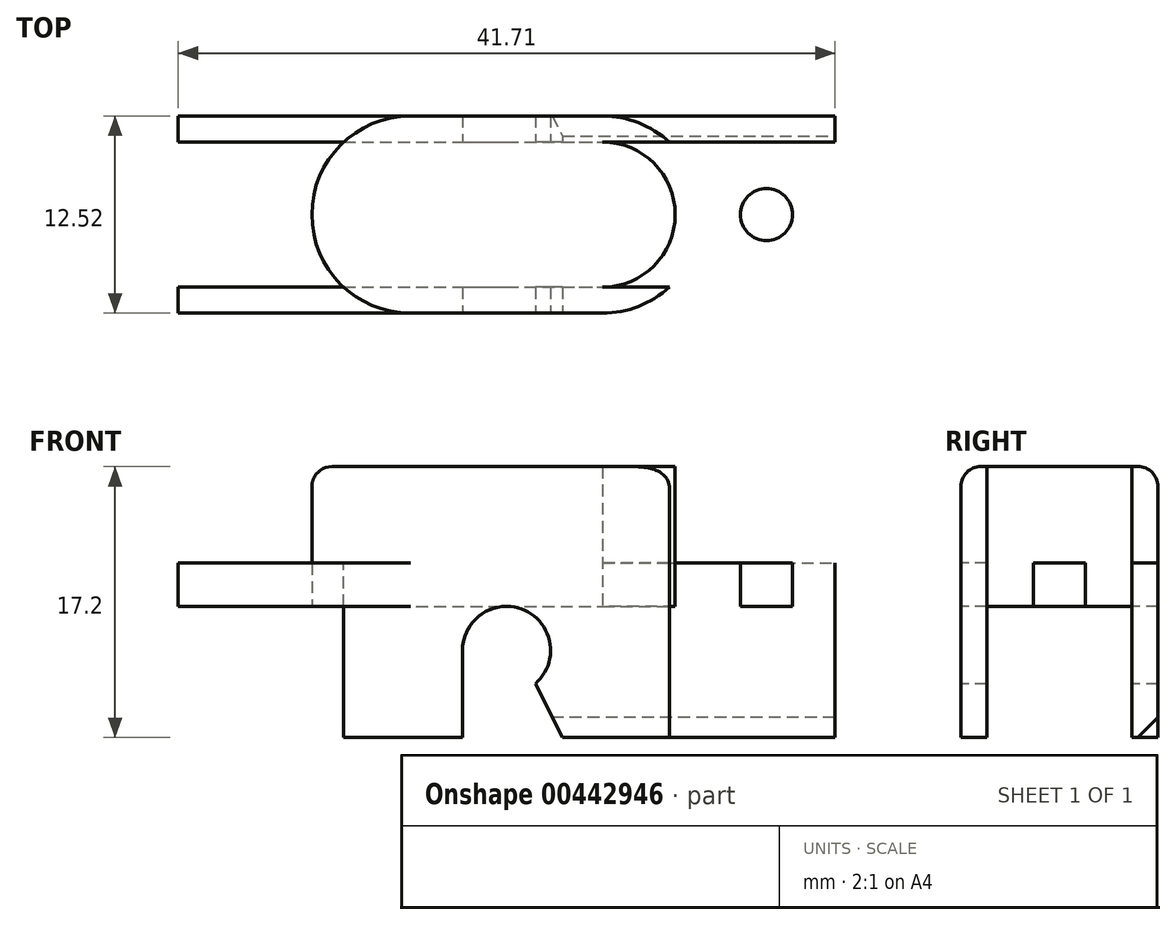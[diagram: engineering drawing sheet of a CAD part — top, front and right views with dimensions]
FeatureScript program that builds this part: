
annotation { "Feature Type Name" : "Feature", "Feature Type Description" : "" }
export const myFeature = defineFeature(function(context is Context, id is Id, definition is map)
    precondition{}
    {
        {
            var Q0;
            Q0=qCreatedBy(makeId("Top.planeOp"),FACE);
            var sketch = newSketch(context, id + "F0", { "sketchPlane" : qUnion([Q0])});
            skLineSegment(sketch, "E0.bottom", {"start": v(0, 12.52) * mm, "end": v(41.7, 12.52) * mm});
            skLineSegment(sketch, "E0.top", {"start": v(0, 0) * mm, "end": v(41.7, 0) * mm});
            skLineSegment(sketch, "E0.left", {"start": v(0, 12.52) * mm, "end": v(0, 0) * mm});
            skLineSegment(sketch, "E0.right", {"start": v(41.7, 12.52) * mm, "end": v(41.7, 0) * mm});
            skCircle(sketch, "E1", {"center": v(4.34, 6.26) * mm, "radius": 1.65 * mm});
            skPoint(sketch, "E2", {"position": v(20.85, 12.52) * mm});
            skPoint(sketch, "E3", {"position": v(20.85, 0) * mm});
            skPoint(sketch, "E4", {"position": v(0, 6.26) * mm});
            skPoint(sketch, "E5", {"position": v(41.7, 6.26) * mm});
            skLineSegment(sketch, "E6.bottom", {"start": v(14.75, 12.52) * mm, "end": v(20.85, 12.52) * mm});
            skLineSegment(sketch, "E6.top", {"start": v(14.75, 0) * mm, "end": v(20.85, 0) * mm});
            skArc(sketch, "E7", {"start": v(14.75, 12.52) * mm, "mid": v(8.49, 6.26) * mm, "end": v(14.75, 0) * mm});
            skPoint(sketch, "E8", {"position": v(8.49, 6.26) * mm});
            skPoint(sketch, "E9", {"position": v(33.22, 6.26) * mm});
            skLineSegment(sketch, "E10", {"start": v(20.85, 12.52) * mm, "end": v(20.85, 0) * mm, "construction": true});
            skLineSegment(sketch, "E11", {"start": v(0, 6.26) * mm, "end": v(41.7, 6.26) * mm, "construction": true});
            skPoint(sketch, "E12", {"position": v(20.85, 6.26) * mm});
            skCircle(sketch, "E13.MirrorC", {"center": v(37.36, 6.26) * mm, "radius": 1.65 * mm});
            skArc(sketch, "E14.0", {"start": v(14.75, 10.87) * mm, "mid": v(10.14, 6.26) * mm, "end": v(14.75, 1.65) * mm});
            skLineSegment(sketch, "E14.1", {"start": v(14.75, 10.87) * mm, "end": v(20.85, 10.87) * mm});
            skLineSegment(sketch, "E14.3", {"start": v(14.75, 1.65) * mm, "end": v(20.85, 1.65) * mm});
            skPoint(sketch, "E15", {"position": v(10.14, 6.26) * mm});
            skLineSegment(sketch, "E16.MirrorCS", {"start": v(26.96, 10.87) * mm, "end": v(20.85, 10.87) * mm});
            skArc(sketch, "E17.MirrorCS", {"start": v(26.96, 10.87) * mm, "mid": v(31.57, 6.26) * mm, "end": v(26.96, 1.65) * mm});
            skLineSegment(sketch, "E18.MirrorCS", {"start": v(26.96, 1.65) * mm, "end": v(20.85, 1.65) * mm});
            skLineSegment(sketch, "E19.MirrorCS", {"start": v(26.96, 0) * mm, "end": v(20.85, 0) * mm});
            skArc(sketch, "E20.MirrorCS", {"start": v(26.96, 12.52) * mm, "mid": v(33.22, 6.26) * mm, "end": v(26.96, 0) * mm});
            skLineSegment(sketch, "E21.MirrorCS", {"start": v(26.96, 12.52) * mm, "end": v(20.85, 12.52) * mm});
            skPoint(sketch, "E22", {"position": v(31.57, 6.26) * mm});
            skPoint(sketch, "E23", {"position": v(41.7, 1.65) * mm});
            skLineSegment(sketch, "E24.top", {"start": v(0, 1.65) * mm, "end": v(41.7, 1.65) * mm});
            skLineSegment(sketch, "E24.left", {"start": v(0, 0) * mm, "end": v(0, 1.65) * mm});
            skLineSegment(sketch, "E24.right", {"start": v(41.7, 0) * mm, "end": v(41.7, 1.65) * mm});
            skLineSegment(sketch, "E25.MirrorCS", {"start": v(0, 12.52) * mm, "end": v(0, 10.87) * mm});
            skLineSegment(sketch, "E26.MirrorCS", {"start": v(0, 10.87) * mm, "end": v(41.7, 10.87) * mm});
            skSolve(sketch);
        }
        {
            var Q0;
            {var subQ0=sQuery(id+"F0.wireOp",EDGE,"E0.top");var subQ1=sQuery(id+"F0.wireOp",EDGE,"E7");var subQ2=makeQuery(id+"F0.imprint","INTERSECT",VERTEX,{"derivedFrom":[subQ1,subQ0]});Q0=makeQuery(id+"F0.imprint","IMPRINT",FACE,{"disambiguationData":[TD([[makeQuery(id+"F0.imprint","IMPRINT",EDGE,{"disambiguationData":[TD([[subQ2,1.0]])],"derivedFrom":subQ1}),1.0]])]});}
            var Q1;
            {var subQ5=sQuery(id+"F0.wireOp",EDGE,"E14.0");Q1=makeQuery(id+"F0.imprint","IMPRINT",FACE,{"disambiguationData":[TD([[makeQuery(id+"F0.imprint","IMPRINT",EDGE,{"derivedFrom":subQ5}),-1.0]])]});}
            var Q2;
            {var subQ2=sQuery(id+"F0.wireOp",EDGE,"E7");var subQ4=sQuery(id+"F0.wireOp",EDGE,"E0.bottom");var subQ8=makeQuery(id+"F0.imprint","INTERSECT",VERTEX,{"derivedFrom":[subQ2,subQ4]});Q2=makeQuery(id+"F0.imprint","IMPRINT",FACE,{"disambiguationData":[TD([[makeQuery(id+"F0.imprint","IMPRINT",EDGE,{"disambiguationData":[TD([[subQ8,-1.0]])],"derivedFrom":subQ2}),1.0]])]});}
            var Q3;
            {var subQ0=sQuery(id+"F0.wireOp",EDGE,"E17.MirrorCS");Q3=makeQuery(id+"F0.imprint","IMPRINT",FACE,{"disambiguationData":[TD([[makeQuery(id+"F0.imprint","IMPRINT",EDGE,{"derivedFrom":subQ0}),1.0]])]});}
            extrude(context, id + "F1", {"entities" : qUnion([Q0, Q1, Q2, Q3]), "depth" : 6.13 * mm});
        }
        {
            var Q0;
            {var subQ5=sQuery(id+"F0.wireOp",EDGE,"E24.left");Q0=makeQuery(id+"F0.imprint","IMPRINT",FACE,{"disambiguationData":[TD([[makeQuery(id+"F0.imprint","IMPRINT",EDGE,{"derivedFrom":subQ5}),-1.0]])]});}
            var Q1;
            {var subQ0=sQuery(id+"F0.wireOp",EDGE,"E0.top");var subQ1=sQuery(id+"F0.wireOp",EDGE,"E7");var subQ2=makeQuery(id+"F0.imprint","INTERSECT",VERTEX,{"derivedFrom":[subQ1,subQ0]});Q1=makeQuery(id+"F0.imprint","IMPRINT",FACE,{"disambiguationData":[TD([[makeQuery(id+"F0.imprint","IMPRINT",EDGE,{"disambiguationData":[TD([[subQ2,1.0]])],"derivedFrom":subQ1}),1.0]])]});}
            var Q2;
            {var subQ5=sQuery(id+"F0.wireOp",EDGE,"E24.right");Q2=makeQuery(id+"F0.imprint","IMPRINT",FACE,{"disambiguationData":[TD([[makeQuery(id+"F0.imprint","IMPRINT",EDGE,{"derivedFrom":subQ5}),1.0]])]});}
            var Q3;
            {var subQ5=sQuery(id+"F0.wireOp",EDGE,"E25.MirrorCS");Q3=makeQuery(id+"F0.imprint","IMPRINT",FACE,{"disambiguationData":[TD([[makeQuery(id+"F0.imprint","IMPRINT",EDGE,{"derivedFrom":subQ5}),1.0]])]});}
            var Q4;
            {var subQ2=sQuery(id+"F0.wireOp",EDGE,"E7");var subQ4=sQuery(id+"F0.wireOp",EDGE,"E0.bottom");var subQ8=makeQuery(id+"F0.imprint","INTERSECT",VERTEX,{"derivedFrom":[subQ2,subQ4]});Q4=makeQuery(id+"F0.imprint","IMPRINT",FACE,{"disambiguationData":[TD([[makeQuery(id+"F0.imprint","IMPRINT",EDGE,{"disambiguationData":[TD([[subQ8,-1.0]])],"derivedFrom":subQ2}),1.0]])]});}
            var Q5;
            {var subQ0=sQuery(id+"F0.wireOp",EDGE,"E0.bottom");var subQ1=sQuery(id+"F0.wireOp",EDGE,"E0.right");var subQ2=makeQuery(id+"F0.imprint","INTERSECT",VERTEX,{"derivedFrom":[subQ1,subQ0]});Q5=makeQuery(id+"F0.imprint","IMPRINT",FACE,{"disambiguationData":[TD([[makeQuery(id+"F0.imprint","IMPRINT",EDGE,{"disambiguationData":[TD([[subQ2,-1.0]])],"derivedFrom":subQ1}),-1.0]])]});}
            extrude(context, id + "F2", {"entities" : qUnion([Q0, Q1, Q2, Q3, Q4, Q5]), "operationType" : NewBodyOperationType.ADD, "oppositeDirection" : true, "depth" : 11.07 * mm});
        }
        {
            var Q0;
            {var subQ5=sQuery(id+"F0.wireOp",EDGE,"E14.0");Q0=makeQuery(id+"F0.imprint","IMPRINT",FACE,{"disambiguationData":[TD([[makeQuery(id+"F0.imprint","IMPRINT",EDGE,{"derivedFrom":subQ5}),-1.0]])]});}
            var Q1;
            {var subQ1=sQuery(id+"F0.wireOp",EDGE,"E0.left");Q1=makeQuery(id+"F0.imprint","IMPRINT",FACE,{"disambiguationData":[TD([[makeQuery(id+"F0.imprint","IMPRINT",EDGE,{"derivedFrom":subQ1}),1.0]])]});}
            var Q2;
            {var subQ0=sQuery(id+"F0.wireOp",EDGE,"E17.MirrorCS");Q2=makeQuery(id+"F0.imprint","IMPRINT",FACE,{"disambiguationData":[TD([[makeQuery(id+"F0.imprint","IMPRINT",EDGE,{"derivedFrom":subQ0}),1.0]])]});}
            var Q3;
            Q3=makeQuery(id+"F0.imprint","IMPRINT",FACE,{"disambiguationData":[TD([[makeQuery(id+"F0.imprint","IMPRINT",EDGE,{"derivedFrom":sQuery(id+"F0.wireOp",EDGE,"E13.MirrorC")}),1.0]])]});
            extrude(context, id + "F3", {"entities" : qUnion([Q0, Q1, Q2, Q3]), "operationType" : NewBodyOperationType.ADD, "oppositeDirection" : true, "depth" : 2.74 * mm});
        }
        {
            var Q0;
            Q0=qCreatedBy(makeId("Front.planeOp"),FACE);
            var sketch = newSketch(context, id + "F4", { "sketchPlane" : qUnion([Q0])});
            skLineSegment(sketch, "E27.bottom", {"start": v(0, 0) * mm, "end": v(41.7, 0) * mm});
            skLineSegment(sketch, "E27.top", {"start": v(0, -11.07) * mm, "end": v(41.7, -11.07) * mm});
            skLineSegment(sketch, "E27.left", {"start": v(0, 0) * mm, "end": v(0, -11.07) * mm});
            skLineSegment(sketch, "E27.right", {"start": v(41.7, 0) * mm, "end": v(41.7, -11.07) * mm});
            skLineSegment(sketch, "E28", {"start": v(0, -2.74) * mm, "end": v(41.7, -2.74) * mm});
            skPoint(sketch, "E29", {"position": v(20.85, -2.74) * mm});
            skCircle(sketch, "E30", {"center": v(20.85, -5.54) * mm, "radius": 2.8 * mm});
            skPoint(sketch, "E30.centerSnap0", {"position": v(20.85, 0) * mm});
            skLineSegment(sketch, "E31", {"start": v(18.06, -11.07) * mm, "end": v(18.06, -5.54) * mm});
            skLineSegment(sketch, "E32", {"start": v(18.06, -5.54) * mm, "end": v(22.68, -7.65) * mm});
            skLineSegment(sketch, "E33", {"start": v(22.68, -7.65) * mm, "end": v(24.4, -11.07) * mm});
            skSolve(sketch);
        }
        {
            var Q0;
            {var subQ0=sQuery(id+"F4.wireOp",EDGE,"E32");Q0=makeQuery(id+"F4.imprint","IMPRINT",FACE,{"disambiguationData":[TD([[makeQuery(id+"F4.imprint","IMPRINT",EDGE,{"derivedFrom":subQ0}),1.0]])]});}
            var Q1;
            {var subQ0=sQuery(id+"F4.wireOp",EDGE,"E32");Q1=makeQuery(id+"F4.imprint","IMPRINT",FACE,{"disambiguationData":[TD([[makeQuery(id+"F4.imprint","IMPRINT",EDGE,{"derivedFrom":subQ0}),-1.0]])]});}
            var Q2;
            {var subQ0=sQuery(id+"F4.wireOp",EDGE,"E31");Q2=makeQuery(id+"F4.imprint","IMPRINT",FACE,{"disambiguationData":[TD([[makeQuery(id+"F4.imprint","IMPRINT",EDGE,{"derivedFrom":subQ0}),-1.0]])]});}
            extrude(context, id + "F5", {"entities" : qUnion([Q0, Q1, Q2]), "operationType" : NewBodyOperationType.REMOVE, "endBound" : BoundingType.THROUGH_ALL, "oppositeDirection" : true, "depth" : 25.4 * mm});
        }
        {
            var Q0;
            {var subQ0=sQuery(id+"F0.wireOp",EDGE,"E24.left");var subQ1=sQuery(id+"F0.wireOp",EDGE,"E0.top");Q0=makeQuery(id+"F5.boolean.opBoolean","SPLIT",EDGE,{"disambiguationData":[TD([makeQuery(id+"F2.opExtrude","SWEPT_FACE",FACE,{"disambiguationData":[OSD([subQ0])]})])],"derivedFrom":makeQuery(id+"F2.opExtrude","CAP_EDGE",EDGE,{"disambiguationData":[OSD([subQ1])],"isStart":false})});}
            var Q1;
            {var subQ0=sQuery(id+"F0.wireOp",EDGE,"E0.top");var subQ2=sQuery(id+"F0.wireOp",EDGE,"E0.right");Q1=makeQuery(id+"F5.boolean.opBoolean","SPLIT",EDGE,{"disambiguationData":[TD([makeQuery(id+"F2.opExtrude","SWEPT_FACE",FACE,{"disambiguationData":[OSD([subQ2])]})])],"derivedFrom":makeQuery(id+"F2.opExtrude","CAP_EDGE",EDGE,{"disambiguationData":[OSD([subQ0])],"isStart":false})});}
            var Q2;
            {var subQ0=sQuery(id+"F0.wireOp",EDGE,"E0.bottom");Q2=makeQuery(id+"F5.boolean.opBoolean","SPLIT",EDGE,{"disambiguationData":[TD([makeQuery(id+"F2.opExtrude","SWEPT_FACE",FACE,{"disambiguationData":[OSD([sQuery(id+"F0.wireOp",EDGE,"E24.left")])]})])],"derivedFrom":makeQuery(id+"F2.opExtrude","CAP_EDGE",EDGE,{"disambiguationData":[OSD([subQ0])],"isStart":false})});}
            var Q3;
            {var subQ0=sQuery(id+"F0.wireOp",EDGE,"E0.right");var subQ1=sQuery(id+"F0.wireOp",EDGE,"E0.bottom");Q3=makeQuery(id+"F5.boolean.opBoolean","SPLIT",EDGE,{"disambiguationData":[TD([makeQuery(id+"F2.opExtrude","SWEPT_FACE",FACE,{"disambiguationData":[OSD([subQ0])]})])],"derivedFrom":makeQuery(id+"F2.opExtrude","CAP_EDGE",EDGE,{"disambiguationData":[OSD([subQ1])],"isStart":false})});}
            chamfer(context, id + "F6", {"entities" : qUnion([Q0, Q1, Q2, Q3]), "width" : 1.27 * mm, "tangentPropagation" : true});
        }
        {
            var Q0;
            Q0=makeQuery(id+"F1.opExtrude","CAP_EDGE",EDGE,{"disambiguationData":[OSD([sQuery(id+"F0.wireOp",EDGE,"E20.MirrorCS")])],"isStart":false});
            var Q1;
            Q1=makeQuery(id+"F1.opExtrude","CAP_EDGE",EDGE,{"disambiguationData":[OSD([sQuery(id+"F0.wireOp",EDGE,"E0.bottom")])],"isStart":false});
            fillet(context, id + "F7", {"entities" : qUnion([Q0, Q1]), "radius" : 1.27 * mm, "tangentPropagation" : true, "allowEdgeOverflow" : false});
        }
    });
